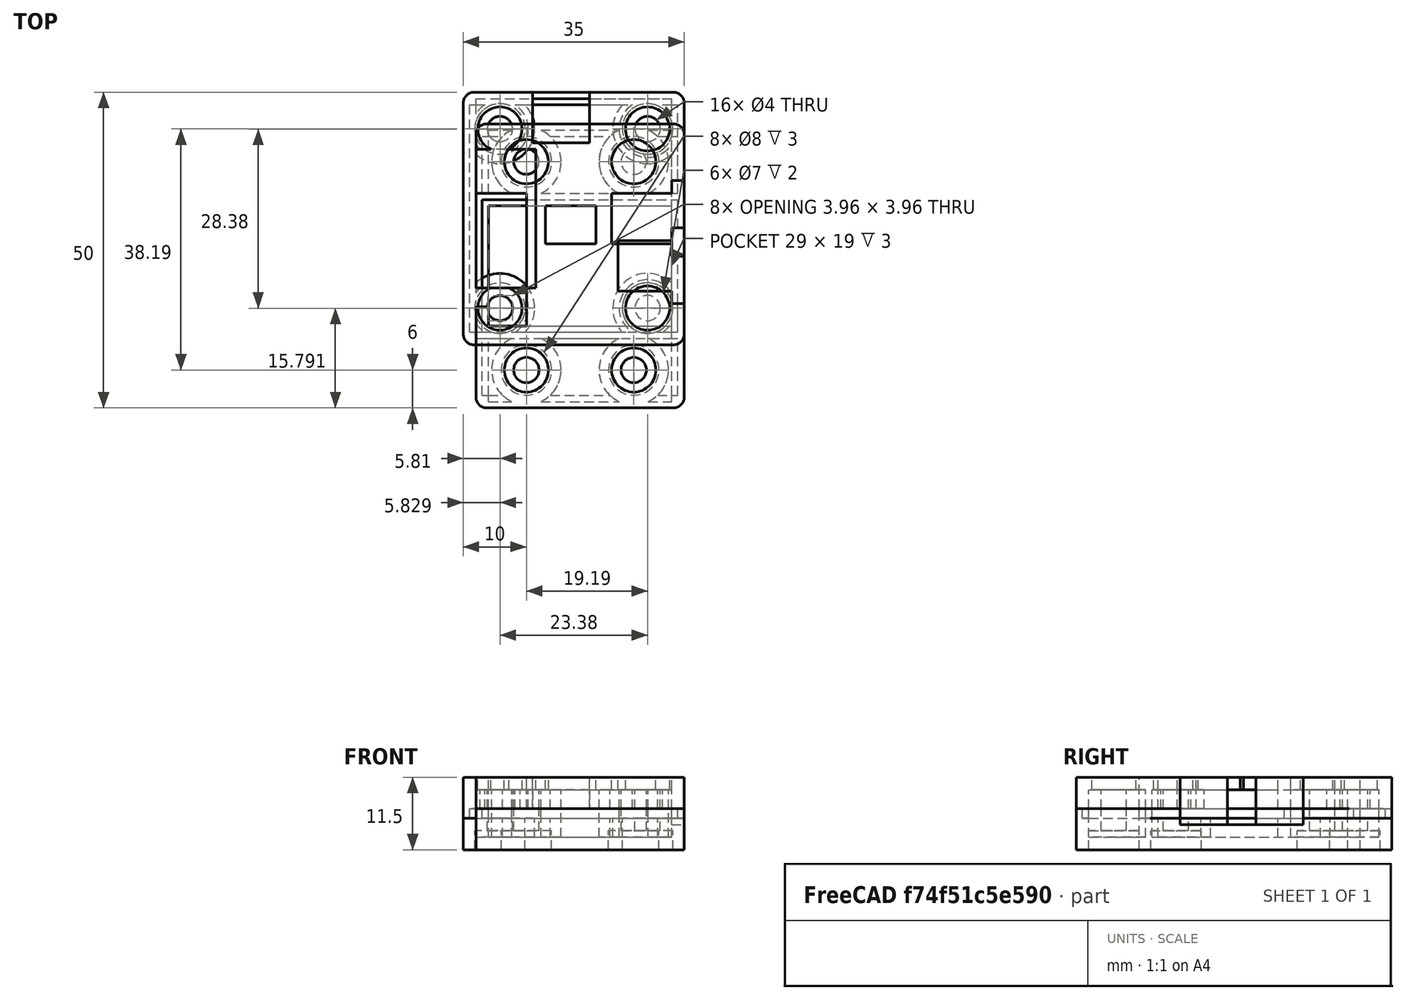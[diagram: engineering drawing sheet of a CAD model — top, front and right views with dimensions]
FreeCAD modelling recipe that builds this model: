
FCSTD DOCUMENT  (FreeCAD 0.14R3700 (Git))
Label: Enclosure
License: CC-BY 3.0
LicenseURL: http://creativecommons.org/licenses/by/3.0/
objects: Part::Box×62, Part::Cylinder×48, Part::Cut×43, Part::MultiFuse×6, Part::Fillet×4, App::DocumentObjectGroup×4
note: 163 computed .brp shape members not serialized (recipe doc carries the construction recipe); baked Part::Feature solids carry a one-line shape summary decoded from their .brp

FEATURE [Part::Box] Box  label="Cube"
  Height = 2
  Length = 31
  Width = 36
FEATURE [Part::Box] Box001  label="Cube001"
  Height = 5
  Length = 31
  Placement = pos=(0,-2,0) rot=(0,0,1;0rad)
  Width = 2
FEATURE [Part::Box] Box002  label="Cube002"
  Height = 5
  Length = 31
  Placement = pos=(0,36,0) rot=(0,0,1;0rad)
  Width = 2
FEATURE [Part::Cylinder] Cylinder
  Angle = 360
  Height = 5
  Placement = pos=(3.81,3.81,0) rot=(0,0,1;0rad)
  Radius = 2
FEATURE [Part::Box] Box003  label="Cube003"
  Height = 5
  Length = 2
  Placement = pos=(-2,-2,0) rot=(0,0,1;0rad)
  Width = 40
FEATURE [Part::Box] Box004  label="Cube004"
  Height = 5
  Length = 2
  Placement = pos=(31,-2,0) rot=(0,0,1;0rad)
  Width = 40
FEATURE [Part::Cylinder] Cylinder001
  Angle = 360
  Height = 5
  Placement = pos=(27.19,32.19,0) rot=(0,0,1;0rad)
  Radius = 2
FEATURE [Part::Cylinder] Cylinder002
  Angle = 360
  Height = 5
  Placement = pos=(3.81,32.19,0) rot=(0,0,1;0rad)
  Radius = 2
FEATURE [Part::Cylinder] Cylinder003
  Angle = 360
  Height = 5
  Placement = pos=(27.19,3.81,0) rot=(0,0,1;0rad)
  Radius = 2
FEATURE [Part::Cylinder] Cylinder004
  Angle = 360
  Height = 5
  Placement = pos=(3.81,3.81,0) rot=(0,0,1;0rad)
  Radius = 5.5
FEATURE [Part::Cylinder] Cylinder005
  Angle = 360
  Height = 5
  Placement = pos=(27.19,3.81,0) rot=(0,0,1;0rad)
  Radius = 5.5
FEATURE [Part::Cylinder] Cylinder006
  Angle = 360
  Height = 5
  Placement = pos=(3.81,32.19,0) rot=(0,0,1;0rad)
  Radius = 5.5
FEATURE [Part::Cylinder] Cylinder007
  Angle = 360
  Height = 5
  Placement = pos=(27.19,32.19,0) rot=(0,0,1;0rad)
  Radius = 5.5
FEATURE [Part::Cylinder] Cylinder008
  Angle = 360
  Height = 3
  Placement = pos=(3.81,3.81,0) rot=(0,0,1;0rad)
  Radius = 4
FEATURE [Part::Cylinder] Cylinder009
  Angle = 360
  Height = 3
  Placement = pos=(3.81,32.19,0) rot=(0,0,1;0rad)
  Radius = 4
FEATURE [Part::Cylinder] Cylinder010
  Angle = 360
  Height = 3
  Placement = pos=(27.19,32.19,0) rot=(0,0,1;0rad)
  Radius = 4
FEATURE [Part::Cylinder] Cylinder011
  Angle = 360
  Height = 3
  Placement = pos=(27.19,3.81,0) rot=(0,0,1;0rad)
  Radius = 4
FEATURE [Part::Cylinder] Cylinder012
  Angle = 360
  Height = 5
  Placement = pos=(3.81,3.81,6.5) rot=(0,0,1;0rad)
  Radius = 4.5
FEATURE [Part::Box] Box005  label="Cube005"
  Height = 1.5
  Length = 31
  Placement = pos=(0,-2,5) rot=(0,0,1;0rad)
  Width = 1
FEATURE [Part::Box] Box006  label="Cube006"
  Height = 1.5
  Length = 31
  Placement = pos=(0,37,5) rot=(0,0,1;0rad)
  Width = 1
FEATURE [Part::Box] Box007  label="Cube007"
  Height = 1.5
  Length = 1
  Placement = pos=(-2,0,5) rot=(0,0,1;0rad)
  Width = 36
FEATURE [Part::Box] Box008  label="Cube008"
  Height = 1.5
  Length = 1
  Placement = pos=(32,0,5) rot=(0,0,1;0rad)
  Width = 14
FEATURE [Part::Box] Box009  label="Cube009"
  Height = 1.5
  Length = 1
  Placement = pos=(32,22,5) rot=(0,0,1;0rad)
  Width = 14
FEATURE [Part::Cylinder] Cylinder013
  Angle = 360
  Height = 5
  Placement = pos=(3.81,32.19,6.5) rot=(0,0,1;0rad)
  Radius = 4.5
FEATURE [Part::Cylinder] Cylinder014
  Angle = 360
  Height = 5
  Placement = pos=(27.19,3.81,6.5) rot=(0,0,1;0rad)
  Radius = 4.5
FEATURE [Part::Cylinder] Cylinder015
  Angle = 360
  Height = 5
  Placement = pos=(27.19,32.19,6.5) rot=(0,0,1;0rad)
  Radius = 4.5
FEATURE [Part::Cylinder] Cylinder016
  Angle = 360
  Height = 5
  Placement = pos=(3.81,3.81,6.5) rot=(0,0,1;0rad)
  Radius = 2
FEATURE [Part::Cylinder] Cylinder017
  Angle = 360
  Height = 5
  Placement = pos=(27.19,32.19,6.5) rot=(0,0,1;0rad)
  Radius = 2
FEATURE [Part::Cylinder] Cylinder018
  Angle = 360
  Height = 5
  Placement = pos=(27.19,3.81,6.5) rot=(0,0,1;0rad)
  Radius = 2
FEATURE [Part::Cylinder] Cylinder019
  Angle = 360
  Height = 5
  Placement = pos=(3.81,32.19,6.5) rot=(0,0,1;0rad)
  Radius = 2
FEATURE [Part::Box] Box010  label="Cube010"
  Height = 5
  Length = 31
  Placement = pos=(0,-2,6.5) rot=(0,0,1;0rad)
  Width = 2
FEATURE [Part::Box] Box011  label="Cube011"
  Height = 5
  Length = 2
  Placement = pos=(-2,-2,6.5) rot=(0,0,1;0rad)
  Width = 40
FEATURE [Part::Box] Box012  label="Cube012"
  Height = 5
  Length = 31
  Placement = pos=(0,36,6.5) rot=(0,0,1;0rad)
  Width = 2
FEATURE [Part::Box] Box013  label="Cube013"
  Height = 5
  Length = 2
  Placement = pos=(31,-2,6.5) rot=(0,0,1;0rad)
  Width = 16
FEATURE [Part::Box] Box014  label="Cube014"
  Height = 5
  Length = 2
  Placement = pos=(31,22,6.5) rot=(0,0,1;0rad)
  Width = 16
FEATURE [Part::Box] Box015  label="Cube015"
  Height = 2
  Length = 31
  Placement = pos=(0,0,9.5) rot=(0,0,1;0rad)
  Width = 36
FEATURE [Part::MultiFuse] Fusion
  Shapes = -> [Box002,Box001,Box004,Box003,Box,Cylinder006,Cylinder004,Cylinder005,Cylinder007]
FEATURE [Part::Cut] Cut
  Base = -> Fusion
  Tool = -> Cylinder011
FEATURE [Part::Cut] Cut001
  Base = -> Cut
  Tool = -> Cylinder010
FEATURE [Part::Cut] Cut002
  Base = -> Cut001
  Tool = -> Cylinder009
FEATURE [Part::Cut] Cut003
  Base = -> Cut002
  Tool = -> Cylinder008
FEATURE [Part::Cut] Cut004
  Base = -> Cut003
  Tool = -> Cylinder
FEATURE [Part::Cut] Cut005
  Base = -> Cut004
  Tool = -> Cylinder003
FEATURE [Part::Cut] Cut006
  Base = -> Cut005
  Tool = -> Cylinder001
FEATURE [Part::Cut] Cut007
  Base = -> Cut006
  Tool = -> Cylinder002
FEATURE [Part::Fillet] Fillet
  Base = -> Cut007
  Edges = 4 edges r=1.7: [Edge3,Edge18,Edge55,Edge107]
FEATURE [Part::Cylinder] Cylinder020
  Angle = 360
  Height = 2
  Placement = pos=(27.19,32.19,9.5) rot=(0,0,1;0rad)
  Radius = 3.5
FEATURE [Part::Box] Box016  label="Cube016"
  Height = 1.5
  Length = 2
  Placement = pos=(-2,-2,5) rot=(0,0,1;0rad)
  Width = 2
FEATURE [Part::Box] Box017  label="Cube017"
  Height = 1.5
  Length = 2
  Placement = pos=(31,-2,5) rot=(0,0,1;0rad)
  Width = 2
FEATURE [Part::Box] Box018  label="Cube018"
  Height = 1.5
  Length = 2
  Placement = pos=(-2,36,5) rot=(0,0,1;0rad)
  Width = 2
FEATURE [Part::Box] Box019  label="Cube019"
  Height = 1.5
  Length = 2
  Placement = pos=(31,36,5) rot=(0,0,1;0rad)
  Width = 2
FEATURE [Part::Cylinder] Cylinder021
  Angle = 360
  Height = 2
  Placement = pos=(3.81,32.19,9.5) rot=(0,0,1;0rad)
  Radius = 3.5
FEATURE [Part::Cylinder] Cylinder022
  Angle = 360
  Height = 2
  Placement = pos=(27.19,3.81,9.5) rot=(0,0,1;0rad)
  Radius = 3.5
FEATURE [Part::Cylinder] Cylinder023
  Angle = 360
  Height = 2
  Placement = pos=(3.81,3.81,9.5) rot=(0,0,1;0rad)
  Radius = 3.5
FEATURE [Part::Box] Box020  label="Cube020"
  Height = 10
  Length = 9.5
  Placement = pos=(0,7,2) rot=(0,0,1;0rad)
  Width = 22
FEATURE [Part::Box] Box021  label="Cube021"
  Height = 10
  Length = 9.5
  Placement = pos=(21.5,14,2) rot=(0,0,1;0rad)
  Width = 8
FEATURE [Part::Box] Box022  label="Cube022"
  Height = 10
  Length = 9
  Placement = pos=(9,30,6.5) rot=(0,0,1;0rad)
  Width = 8
FEATURE [Part::MultiFuse] Fusion002
  Shapes = -> [Box013,Box015,Box010,Box014,Box012,Box011,Cylinder013,Cylinder015,Cylinder014,Cylinder012]
FEATURE [Part::Box] Box023  label="Cube023"
  Height = 10
  Length = 2
  Placement = pos=(31,12,3) rot=(0,0,1;0rad)
  Width = 12
FEATURE [Part::Box] Box024  label="Cube024"
  Height = 10
  Length = 2
  Placement = pos=(31,12,4) rot=(0,0,1;0rad)
  Width = 12
FEATURE [Part::Cut] Cut020  label="RS232_Bottom_Half"
  Base = -> Fillet
  Tool = -> Box024
FEATURE [App::DocumentObjectGroup] Group  label="Bottom_Half"
  Group = -> [Box002,Box001,Box004,Box003,Cylinder006,Cylinder004,Box,Cylinder005,Cylinder007,Cylinder011,Cylinder010,Cylinder009,Cylinder008,Cylinder,Cylinder003,Cylinder001,Cylinder002,Fillet,Cut020]
FEATURE [Part::Box] Box025  label="Cube025"
  Height = 2
  Length = 33
  Width = 21
FEATURE [Part::Box] Box026  label="Cube026"
  Height = 2
  Length = 33
  Placement = pos=(0,-12,0) rot=(0,0,1;0rad)
  Width = 12
FEATURE [Part::Cylinder] Cylinder024
  Angle = 360
  Height = 6.5
  Placement = pos=(8,-6,0) rot=(0,0,1;0rad)
  Radius = 2
FEATURE [Part::Box] Box027  label="Cube027"
  Height = 3
  Length = 33
  Placement = pos=(0,-1,2) rot=(0,0,1;0rad)
  Width = 2
FEATURE [Part::Box] Box028  label="Cube028"
  Height = 3
  Length = 33
  Placement = pos=(0,20,2) rot=(0,0,1;0rad)
  Width = 2
FEATURE [Part::Box] Box029  label="Cube029"
  Height = 2
  Length = 33
  Placement = pos=(0,21,0) rot=(0,0,1;0rad)
  Width = 12
FEATURE [Part::Cylinder] Cylinder025
  Angle = 360
  Height = 6.5
  Placement = pos=(8,-6,0) rot=(0,0,1;0rad)
  Radius = 5.5
FEATURE [Part::Cylinder] Cylinder026
  Angle = 360
  Height = 3
  Placement = pos=(8,-6,0) rot=(0,0,1;0rad)
  Radius = 4
FEATURE [Part::Cylinder] Cylinder027
  Angle = 360
  Height = 6.5
  Placement = pos=(8,27,0) rot=(0,0,1;0rad)
  Radius = 5.5
FEATURE [Part::Cylinder] Cylinder028
  Angle = 360
  Height = 6.5
  Placement = pos=(25,-6,0) rot=(0,0,1;0rad)
  Radius = 5.5
FEATURE [Part::Cylinder] Cylinder029
  Angle = 360
  Height = 6.5
  Placement = pos=(25,27,0) rot=(0,0,1;0rad)
  Radius = 5.5
FEATURE [Part::Cylinder] Cylinder030
  Angle = 360
  Height = 3
  Placement = pos=(8,27,0) rot=(0,0,1;0rad)
  Radius = 4
FEATURE [Part::Cylinder] Cylinder031
  Angle = 360
  Height = 3
  Placement = pos=(25,27,0) rot=(0,0,1;0rad)
  Radius = 4
FEATURE [Part::Cylinder] Cylinder032
  Angle = 360
  Height = 3
  Placement = pos=(25,-6,0) rot=(0,0,1;0rad)
  Radius = 4
FEATURE [Part::Cylinder] Cylinder033
  Angle = 360
  Height = 6.5
  Placement = pos=(25,-6,0) rot=(0,0,1;0rad)
  Radius = 2
FEATURE [Part::Cylinder] Cylinder034
  Angle = 360
  Height = 6.5
  Placement = pos=(25,27,0) rot=(0,0,1;0rad)
  Radius = 2
FEATURE [Part::Cylinder] Cylinder035
  Angle = 360
  Height = 6.5
  Placement = pos=(8,27,0) rot=(0,0,1;0rad)
  Radius = 2
FEATURE [Part::Box] Box030  label="Cube030"
  Height = 3
  Length = 33
  Placement = pos=(0,-12,2) rot=(0,0,1;0rad)
  Width = 2
FEATURE [Part::Box] Box031  label="Cube031"
  Height = 3
  Length = 33
  Placement = pos=(0,31,2) rot=(0,0,1;0rad)
  Width = 2
FEATURE [Part::Box] Box032  label="Cube032"
  Height = 3
  Length = 2
  Placement = pos=(0,1,2) rot=(0,0,1;0rad)
  Width = 19
FEATURE [Part::Box] Box033  label="Cube033"
  Height = 3
  Length = 2
  Placement = pos=(31,1,2) rot=(0,0,1;0rad)
  Width = 19
FEATURE [Part::Box] Box034  label="Cube034"
  Height = 3
  Length = 2
  Placement = pos=(0,-10,2) rot=(0,0,1;0rad)
  Width = 9
FEATURE [Part::Box] Box035  label="Cube035"
  Height = 3
  Length = 2
  Placement = pos=(0,22,2) rot=(0,0,1;0rad)
  Width = 9
FEATURE [Part::Box] Box036  label="Cube036"
  Height = 3
  Length = 2
  Placement = pos=(31,22,2) rot=(0,0,1;0rad)
  Width = 9
FEATURE [Part::Box] Box037  label="Cube037"
  Height = 3
  Length = 2
  Placement = pos=(31,-10,2) rot=(0,0,1;0rad)
  Width = 9
FEATURE [Part::Box] Box038  label="Cube038"
  Height = 1.5
  Length = 29
  Placement = pos=(2,-12,5) rot=(0,0,1;0rad)
  Width = 1
FEATURE [Part::Box] Box039  label="Cube039"
  Height = 1.5
  Length = 31
  Placement = pos=(1,-1,5) rot=(0,0,1;0rad)
  Width = 1
FEATURE [Part::Box] Box040  label="Cube040"
  Height = 1.5
  Length = 29
  Placement = pos=(2,32,5) rot=(0,0,1;0rad)
  Width = 1
FEATURE [Part::Box] Box041  label="Cube041"
  Height = 1.5
  Length = 31
  Placement = pos=(1,21,5) rot=(0,0,1;0rad)
  Width = 1
FEATURE [Part::Box] Box042  label="Cube042"
  Height = 1.5
  Length = 1
  Placement = pos=(0,-10,5) rot=(0,0,1;0rad)
  Width = 41
FEATURE [Part::Box] Box043  label="Cube043"
  Height = 1.5
  Length = 1
  Placement = pos=(32,-10,5) rot=(0,0,1;0rad)
  Width = 41
FEATURE [Part::Box] Box044  label="Cube044"
  Height = 1.5
  Length = 2
  Placement = pos=(0,-12,5) rot=(0,0,1;0rad)
  Width = 2
FEATURE [Part::Box] Box045  label="Cube045"
  Height = 1.5
  Length = 2
  Placement = pos=(31,-12,5) rot=(0,0,1;0rad)
  Width = 2
FEATURE [Part::Box] Box046  label="Cube046"
  Height = 1.5
  Length = 2
  Placement = pos=(0,31,5) rot=(0,0,1;0rad)
  Width = 2
FEATURE [Part::Box] Box047  label="Cube047"
  Height = 1.5
  Length = 2
  Placement = pos=(31,31,5) rot=(0,0,1;0rad)
  Width = 2
FEATURE [Part::Box] Box048  label="Cube048"
  Height = 3
  Length = 2
  Placement = pos=(31,4.5,4) rot=(0,0,1;0rad)
  Width = 12
FEATURE [Part::Cylinder] Cylinder036
  Angle = 360
  Height = 5
  Placement = pos=(8,-6,6.5) rot=(0,0,1;0rad)
  Radius = 5.5
FEATURE [Part::Cylinder] Cylinder037
  Angle = 360
  Height = 5
  Placement = pos=(25,27,6.5) rot=(0,0,1;0rad)
  Radius = 5.5
FEATURE [Part::Cylinder] Cylinder038
  Angle = 360
  Height = 5
  Placement = pos=(25,-6,6.5) rot=(0,0,1;0rad)
  Radius = 5.5
FEATURE [Part::Cylinder] Cylinder039
  Angle = 360
  Height = 5
  Placement = pos=(8,27,6.5) rot=(0,0,1;0rad)
  Radius = 5.5
FEATURE [Part::Cylinder] Cylinder040
  Angle = 360
  Height = 5
  Placement = pos=(8,27,6.5) rot=(0,0,1;0rad)
  Radius = 2
FEATURE [Part::Cylinder] Cylinder041
  Angle = 360
  Height = 5
  Placement = pos=(25,27,6.5) rot=(0,0,1;0rad)
  Radius = 2
FEATURE [Part::Cylinder] Cylinder042
  Angle = 360
  Height = 5
  Placement = pos=(25,-6,6.5) rot=(0,0,1;0rad)
  Radius = 2
FEATURE [Part::Cylinder] Cylinder043
  Angle = 360
  Height = 5
  Placement = pos=(8,-6,6.5) rot=(0,0,1;0rad)
  Radius = 2
FEATURE [Part::Cylinder] Cylinder044
  Angle = 360
  Height = 2
  Placement = pos=(8,-6,9.5) rot=(0,0,1;0rad)
  Radius = 3.5
FEATURE [Part::Cylinder] Cylinder045
  Angle = 360
  Height = 2
  Placement = pos=(8,27,9.5) rot=(0,0,1;0rad)
  Radius = 3.5
FEATURE [Part::Cylinder] Cylinder046
  Angle = 360
  Height = 2
  Placement = pos=(25,27,9.5) rot=(0,0,1;0rad)
  Radius = 3.5
FEATURE [Part::Cylinder] Cylinder047
  Angle = 360
  Height = 2
  Placement = pos=(25,-6,9.5) rot=(0,0,1;0rad)
  Radius = 3.5
FEATURE [Part::Box] Box049  label="Cube049"
  Height = 2
  Length = 33
  Placement = pos=(0,-12,9.5) rot=(0,0,1;0rad)
  Width = 45
FEATURE [Part::MultiFuse] Fusion004
  Shapes = -> [Box025,Box026,Box027,Box028,Box029,Cylinder025,Cylinder027,Cylinder028,Cylinder029,Box030,Box031,Box032,Box033,Box034,Box035,Box036,Box037,Box038,Box039,Box040,Box041,Box042,Box043,Box044,Box045,Box046,Box047]
FEATURE [Part::Cut] Cut021
  Base = -> Fusion004
  Tool = -> Cylinder035
FEATURE [Part::Cut] Cut022
  Base = -> Cut021
  Tool = -> Cylinder034
FEATURE [Part::Cut] Cut023
  Base = -> Cut022
  Tool = -> Cylinder033
FEATURE [Part::Cut] Cut024
  Base = -> Cut023
  Tool = -> Cylinder032
FEATURE [Part::Cut] Cut025
  Base = -> Cut024
  Tool = -> Cylinder031
FEATURE [Part::Cut] Cut026
  Base = -> Cut025
  Tool = -> Cylinder030
FEATURE [Part::Cut] Cut027
  Base = -> Cut026
  Tool = -> Cylinder024
FEATURE [Part::Cut] Cut028
  Base = -> Cut027
  Tool = -> Cylinder026
FEATURE [Part::Cut] Cut029
  Base = -> Cut028
  Tool = -> Box048
FEATURE [Part::Fillet] Fillet006  label="RS485_Bottom_Half"
  Base = -> Cut029
  Edges = 12 edges r=1.7: [Edge13,Edge18,Edge31,Edge42,Edge68,Edge72,Edge85,Edge90,Edge131,Edge139,Edge152,Edge247]
FEATURE [App::DocumentObjectGroup] Group002  label="RS485_Bottom"
  Group = -> [Fillet006]
FEATURE [Part::Box] Box050  label="Cube050"
  Height = 3
  Length = 2
  Placement = pos=(0,-12,6.5) rot=(0,0,1;0rad)
  Width = 16
FEATURE [Part::Box] Box051  label="Cube051"
  Height = 3
  Length = 2
  Placement = pos=(0,22,6.5) rot=(0,0,1;0rad)
  Width = 11
FEATURE [Part::Box] Box052  label="Cube052"
  Height = 3
  Length = 31
  Placement = pos=(2,31,6.5) rot=(0,0,1;0rad)
  Width = 2
FEATURE [Part::Box] Box053  label="Cube053"
  Height = 3
  Length = 31
  Placement = pos=(2,-12,6.5) rot=(0,0,1;0rad)
  Width = 2
FEATURE [Part::Box] Box054  label="Cube054"
  Height = 3
  Length = 2
  Placement = pos=(31,-10,6.5) rot=(0,0,1;0rad)
  Width = 41
FEATURE [Part::Box] Box055  label="Cube055"
  Height = 3
  Length = 29
  Placement = pos=(2,-1,6.5) rot=(0,0,1;0rad)
  Width = 2
FEATURE [Part::Box] Box056  label="Cube056"
  Height = 3
  Length = 23
  Placement = pos=(8,20,6.5) rot=(0,0,1;0rad)
  Width = 2
FEATURE [Part::Box] Box057  label="Cube057"
  Height = 5
  Length = 8
  Placement = pos=(0,4,6.5) rot=(0,0,1;0rad)
  Width = 18
FEATURE [Part::Box] Box058  label="Cube058"
  Height = 2
  Length = 6
  Placement = pos=(2,1,9.5) rot=(0,0,1;0rad)
  Width = 3
FEATURE [Part::Box] Box059  label="Cube059"
  Height = 5
  Length = 2
  Placement = pos=(31,4.5,6.5) rot=(0,0,1;0rad)
  Width = 12
FEATURE [Part::Box] Box060  label="Cube060"
  Height = 2
  Length = 8
  Placement = pos=(11,14,9.5) rot=(0,0,1;0rad)
  Width = 6
FEATURE [Part::Box] Box061  label="Cube061"
  Height = 2
  Length = 8.5
  Placement = pos=(22.5,6.5,9.5) rot=(0,0,1;0rad)
  Width = 8
FEATURE [Part::MultiFuse] Fusion005
  Shapes = -> [Box051,Box055,Box050,Box052,Box054,Box056,Cylinder036,Cylinder038,Box053,Box049,Cylinder039,Cylinder037]
FEATURE [Part::Cut] Cut030
  Base = -> Fusion005
  Tool = -> Cylinder045
FEATURE [Part::Cut] Cut031
  Base = -> Cut030
  Tool = -> Cylinder043
FEATURE [Part::Cut] Cut032
  Base = -> Cut031
  Tool = -> Cylinder044
FEATURE [Part::Cut] Cut033
  Base = -> Cut032
  Tool = -> Cylinder042
FEATURE [Part::Cut] Cut034
  Base = -> Cut033
  Tool = -> Cylinder041
FEATURE [Part::Cut] Cut035
  Base = -> Cut034
  Tool = -> Cylinder040
FEATURE [Part::Cut] Cut036
  Base = -> Cut035
  Tool = -> Box057
FEATURE [Part::Cut] Cut037
  Base = -> Cut036
  Tool = -> Box058
FEATURE [Part::Cut] Cut038
  Base = -> Cut037
  Tool = -> Box059
FEATURE [Part::Cut] Cut039
  Base = -> Cut038
  Tool = -> Box061
FEATURE [Part::Cut] Cut040
  Base = -> Cut039
  Tool = -> Box060
FEATURE [Part::Cut] Cut041
  Base = -> Cut040
  Tool = -> Cylinder046
FEATURE [Part::Cut] Cut042
  Base = -> Cut041
  Tool = -> Cylinder047
FEATURE [Part::Fillet] Fillet007  label="RS485_Top_Half"
  Base = -> Cut042
  Edges = 8 edges r=1.7: [Edge2,Edge12,Edge14,Edge16,Edge110,Edge116,Edge177,Edge182]
FEATURE [App::DocumentObjectGroup] Group003  label="RS485_Top"
  Group = -> [Fillet007]
FEATURE [Part::MultiFuse] Fusion006
  Shapes = -> [Box018,Box016,Box017,Box019,Box007,Box005,Box008,Box009,Box006]
FEATURE [Part::MultiFuse] Fusion007
  Shapes = -> [Fusion006,Fusion002]
FEATURE [Part::Cut] Cut043
  Base = -> Fusion007
  Tool = -> Box023
FEATURE [Part::Cut] Cut044
  Base = -> Cut043
  Tool = -> Cylinder023
FEATURE [Part::Cut] Cut045
  Base = -> Cut044
  Tool = -> Cylinder022
FEATURE [Part::Cut] Cut046
  Base = -> Cut045
  Tool = -> Cylinder021
FEATURE [Part::Cut] Cut047
  Base = -> Cut046
  Tool = -> Cylinder020
FEATURE [Part::Cut] Cut048
  Base = -> Cut047
  Tool = -> Cylinder019
FEATURE [Part::Cut] Cut049
  Base = -> Cut048
  Tool = -> Box020
FEATURE [Part::Cut] Cut050
  Base = -> Cut049
  Tool = -> Box021
FEATURE [Part::Cut] Cut051
  Base = -> Cut050
  Tool = -> Box022
FEATURE [Part::Cut] Cut052
  Base = -> Cut051
  Tool = -> Cylinder018
FEATURE [Part::Cut] Cut053
  Base = -> Cut052
  Tool = -> Cylinder017
FEATURE [Part::Cut] Cut054
  Base = -> Cut053
  Tool = -> Cylinder016
FEATURE [Part::Fillet] Fillet008  label="RS232_Top_Half"
  Base = -> Cut054
  Edges = 8 edges r=1.7: [Edge9,Edge25,Edge28,Edge63,Edge83,Edge166,Edge258,Edge287]
FEATURE [App::DocumentObjectGroup] Group001  label="Top_Half"
  Group = -> [Fillet008]
